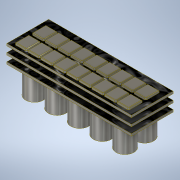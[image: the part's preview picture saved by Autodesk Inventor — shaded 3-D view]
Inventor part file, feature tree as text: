
AUTODESK INVENTOR PART (.ipt)
format: ipt  version: 2020 (Build 240168000, 168)  size: 653,824 bytes
history: native  units: mm
features: chamfer x16, extrude x9, sketch x9, other x2
ambient origin geometry x8: Origin, YZ Plane, XZ Plane, XY Plane, X Axis, Y Axis, Z Axis, Center Point
bodies: Body1 (feature_tree)
feature tree (36):
  other  "Bryła1"
  extrude  "Wyciągnięcie proste1"  Depth=18.73mm
  extrude  "Wyciągnięcie proste2"  Depth=9.365mm
  chamfer  "Faza1"  Distance=55.88mm
  chamfer  "Faza2"  Distance=27.94mm
  chamfer  "Faza3"  Distance=1.0mm
  extrude  "Wyciągnięcie proste3"  Depth=6.03mm
  chamfer  "Faza4"  Distance=5.08mm
  extrude  "Wyciągnięcie proste4"  Depth=2.54mm
  chamfer  "Faza5"  Distance=1.27mm
  chamfer  "Faza6"  Distance=5.08mm
  chamfer  "Faza7"  Distance=6.03mm
  chamfer  "Faza8"  Distance=1.27mm
  chamfer  "Faza9"  Distance=0.64mm
  chamfer  "Faza10"  Distance=5.08mm
  chamfer  "Faza11"  Distance=0.64mm
  chamfer  "Faza12"  Distance=5.08mm
  chamfer  "Faza13"  Distance=0.64mm
  chamfer  "Faza14"  Distance=5.08mm
  chamfer  "Faza15"  Distance=0.64mm
  chamfer  "Faza16"  Distance=5.08mm
  other  "Płaszczyzna konstrukcyjna1"
  extrude  "Wyciągnięcie proste5"  Depth=5.08mm
  extrude  "Wyciągnięcie proste6"  Depth=5.08mm
  extrude  "Wyciągnięcie proste7"  Depth=5.08mm
  extrude  "Wyciągnięcie proste8"  Depth=0.64mm
  extrude  "Wyciągnięcie proste9"  Depth=0.64mm
  sketch  "Szkic1"
  sketch  "Szkic2"
  sketch  "Szkic3"
  sketch  "Szkic4"
  sketch  "Szkic5"
  sketch  "Szkic6"
  sketch  "Szkic7"
  sketch  "Szkic8"
  sketch  "Szkic9"
